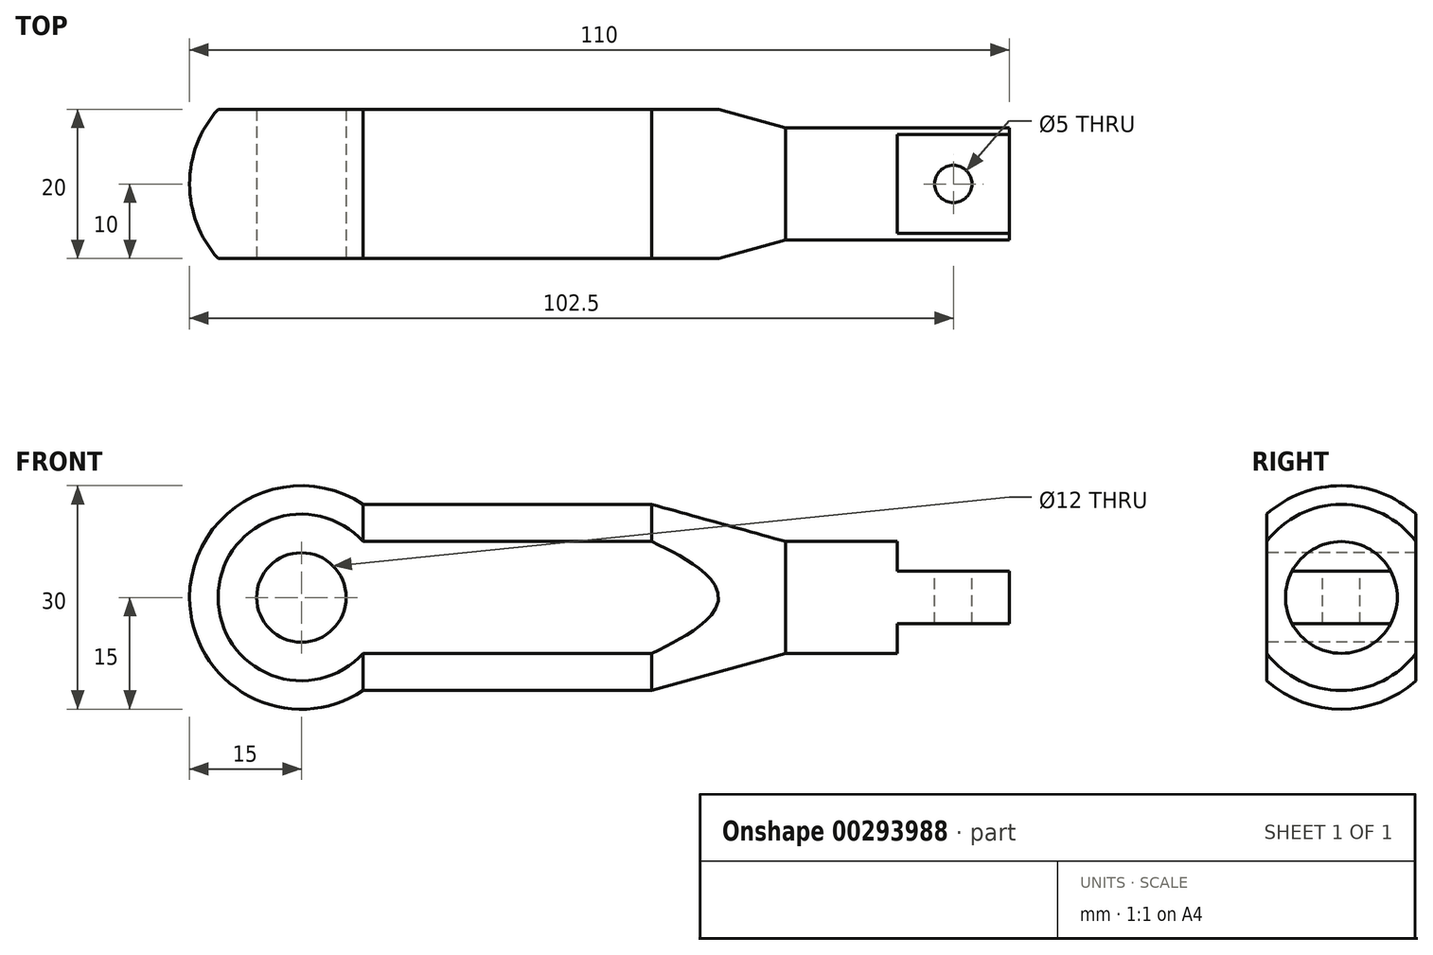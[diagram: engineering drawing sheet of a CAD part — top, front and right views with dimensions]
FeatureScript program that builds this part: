
annotation { "Feature Type Name" : "Feature", "Feature Type Description" : "" }
export const myFeature = defineFeature(function(context is Context, id is Id, definition is map)
    precondition{}
    {
        {
            var Q0;
            Q0=qCreatedBy(makeId("Front.planeOp"),FACE);
            var sketch = newSketch(context, id + "F0", { "sketchPlane" : qUnion([Q0])});
            skArc(sketch, "E0", {"start": v(8.3, 12.5) * mm, "mid": v(-7.1, 13.22) * mm, "end": v(-15, 0) * mm});
            skLineSegment(sketch, "E1", {"start": v(8.3, 12.5) * mm, "end": v(47, 12.5) * mm});
            skLineSegment(sketch, "E2", {"start": v(-15, 0) * mm, "end": v(95, 0) * mm});
            skLineSegment(sketch, "E3", {"start": v(-26.8, 0) * mm, "end": v(114.62, 0) * mm, "construction": true});
            skLineSegment(sketch, "E4", {"start": v(47, 12.5) * mm, "end": v(65, 7.5) * mm});
            skLineSegment(sketch, "E5", {"start": v(65, 7.5) * mm, "end": v(95, 7.5) * mm});
            skLineSegment(sketch, "E6", {"start": v(95, 7.5) * mm, "end": v(95, 0) * mm});
            skSolve(sketch);
        }
        {
            var Q0;
            Q0 = qSketchRegion(id + "F0", true);
            var Q1;
            Q1=sQuery(id+"F0.wireOp",EDGE,"E3");
            revolve(context, id + "F1", {"entities" : qUnion([Q0]), "axis" : qUnion([Q1]), "revolveType" : RevolveType.FULL});
        }
        {
            var Q0;
            Q0=makeQuery(id+"F1.opRevolve","SWEPT_FACE",FACE,{"disambiguationData":[OSD([sQuery(id+"F0.wireOp",EDGE,"E6")])]});
            var sketch = newSketch(context, id + "F2", { "sketchPlane" : qUnion([Q0])});
            skLineSegment(sketch, "E7.bottom", {"start": v(-34.75, 25.13) * mm, "end": v(-10, 25.13) * mm});
            skLineSegment(sketch, "E7.top", {"start": v(-34.75, -27.07) * mm, "end": v(-10, -27.07) * mm});
            skLineSegment(sketch, "E7.left", {"start": v(-34.75, 25.13) * mm, "end": v(-34.75, -27.07) * mm});
            skLineSegment(sketch, "E7.right", {"start": v(-10, 25.13) * mm, "end": v(-10, -27.07) * mm});
            skLineSegment(sketch, "E8.bottom", {"start": v(10, 25.13) * mm, "end": v(32.88, 25.13) * mm});
            skLineSegment(sketch, "E8.top", {"start": v(10, -27.07) * mm, "end": v(32.88, -27.07) * mm});
            skLineSegment(sketch, "E8.left", {"start": v(10, 25.13) * mm, "end": v(10, -27.07) * mm});
            skLineSegment(sketch, "E8.right", {"start": v(32.88, 25.13) * mm, "end": v(32.88, -27.07) * mm});
            skSolve(sketch);
        }
        {
            var Q0;
            Q0 = qSketchRegion(id + "F2", true);
            extrude(context, id + "F3", {"entities" : qUnion([Q0]), "operationType" : NewBodyOperationType.REMOVE, "endBound" : BoundingType.THROUGH_ALL, "oppositeDirection" : true, "depth" : 25 * mm});
        }
        {
            var Q0;
            Q0=makeQuery(id+"F1.opRevolve","SWEPT_FACE",FACE,{"disambiguationData":[OSD([sQuery(id+"F0.wireOp",EDGE,"E6")])]});
            var sketch = newSketch(context, id + "F4", { "sketchPlane" : qUnion([Q0])});
            skLineSegment(sketch, "E9.bottom", {"start": v(-20.2, 17.16) * mm, "end": v(20.63, 17.16) * mm});
            skLineSegment(sketch, "E9.top", {"start": v(-20.2, 3.5) * mm, "end": v(20.63, 3.5) * mm});
            skLineSegment(sketch, "E9.left", {"start": v(-20.2, 17.16) * mm, "end": v(-20.2, 3.5) * mm});
            skLineSegment(sketch, "E9.right", {"start": v(20.63, 17.16) * mm, "end": v(20.63, 3.5) * mm});
            skLineSegment(sketch, "E10.bottom", {"start": v(-20.2, -3.5) * mm, "end": v(20.63, -3.5) * mm});
            skLineSegment(sketch, "E10.top", {"start": v(-20.2, -19.29) * mm, "end": v(20.63, -19.29) * mm});
            skLineSegment(sketch, "E10.left", {"start": v(-20.2, -3.5) * mm, "end": v(-20.2, -19.29) * mm});
            skLineSegment(sketch, "E10.right", {"start": v(20.63, -3.5) * mm, "end": v(20.63, -19.29) * mm});
            skSolve(sketch);
        }
        {
            var Q0;
            Q0 = qSketchRegion(id + "F4", true);
            extrude(context, id + "F5", {"entities" : qUnion([Q0]), "operationType" : NewBodyOperationType.REMOVE, "oppositeDirection" : true, "depth" : 15 * mm});
        }
        {
            var Q0;
            Q0=makeQuery(id+"F5.boolean.opBoolean","COPY",FACE,{"derivedFrom":makeQuery(id+"F5.opExtrude","SWEPT_FACE",FACE,{"disambiguationData":[OSD([sQuery(id+"F4.wireOp",EDGE,"E9.top")])]})});
            var sketch = newSketch(context, id + "F6", { "sketchPlane" : qUnion([Q0])});
            skCircle(sketch, "E11", {"center": v(87.5, 0) * mm, "radius": 2.5 * mm});
            skSolve(sketch);
        }
        {
            var Q0;
            Q0 = qSketchRegion(id + "F6", true);
            extrude(context, id + "F7", {"entities" : qUnion([Q0]), "operationType" : NewBodyOperationType.REMOVE, "endBound" : BoundingType.THROUGH_ALL, "oppositeDirection" : true, "depth" : 25 * mm});
        }
        {
            var Q0;
            Q0=makeQuery(id+"F3.boolean.opBoolean","COPY",FACE,{"derivedFrom":makeQuery(id+"F3.opExtrude","SWEPT_FACE",FACE,{"disambiguationData":[OSD([sQuery(id+"F2.wireOp",EDGE,"E7.right")])]})});
            var sketch = newSketch(context, id + "F8", { "sketchPlane" : qUnion([Q0])});
            skCircle(sketch, "E12", {"center": v(0, 0) * mm, "radius": 6 * mm});
            skSolve(sketch);
        }
        {
            var Q0;
            Q0 = qSketchRegion(id + "F8", true);
            extrude(context, id + "F9", {"entities" : qUnion([Q0]), "operationType" : NewBodyOperationType.REMOVE, "endBound" : BoundingType.THROUGH_ALL, "oppositeDirection" : true, "depth" : 25 * mm});
        }
    });
